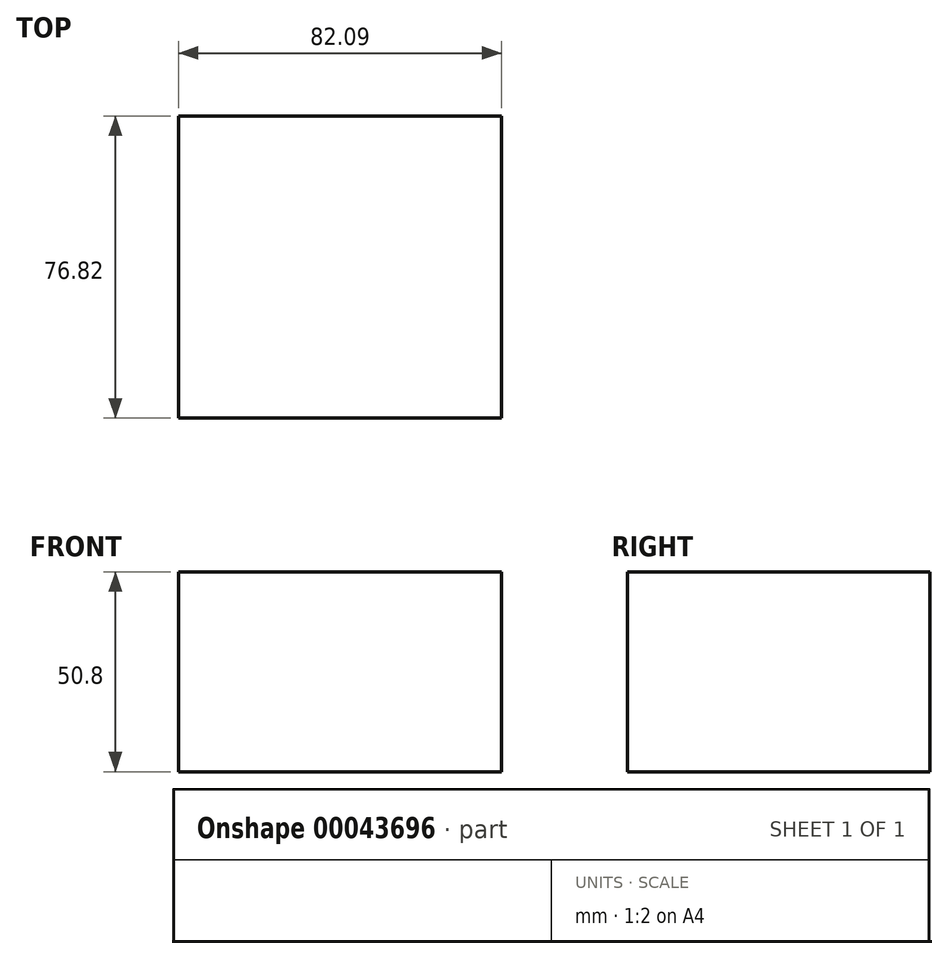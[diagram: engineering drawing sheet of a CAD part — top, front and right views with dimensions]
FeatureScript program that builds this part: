
annotation { "Feature Type Name" : "Feature", "Feature Type Description" : "" }
export const myFeature = defineFeature(function(context is Context, id is Id, definition is map)
    precondition{}
    {
        {
            var Q0;
            Q0=qCreatedBy(makeId("Top.planeOp"),FACE);
            var sketch = newSketch(context, id + "F0", { "sketchPlane" : qUnion([Q0])});
            skLineSegment(sketch, "E0.bottom", {"start": v(-40.21, 40.35) * mm, "end": v(41.88, 40.35) * mm});
            skLineSegment(sketch, "E0.top", {"start": v(-40.21, -36.47) * mm, "end": v(41.88, -36.47) * mm});
            skLineSegment(sketch, "E0.left", {"start": v(-40.21, 40.35) * mm, "end": v(-40.21, -36.47) * mm});
            skLineSegment(sketch, "E0.right", {"start": v(41.88, 40.35) * mm, "end": v(41.88, -36.47) * mm});
            skSolve(sketch);
        }
        {
            var Q0;
            Q0 = qSketchRegion(id + "F0", true);
            extrude(context, id + "F1", {"entities" : qUnion([Q0]), "depth" : 50.8 * mm});
        }
    });
